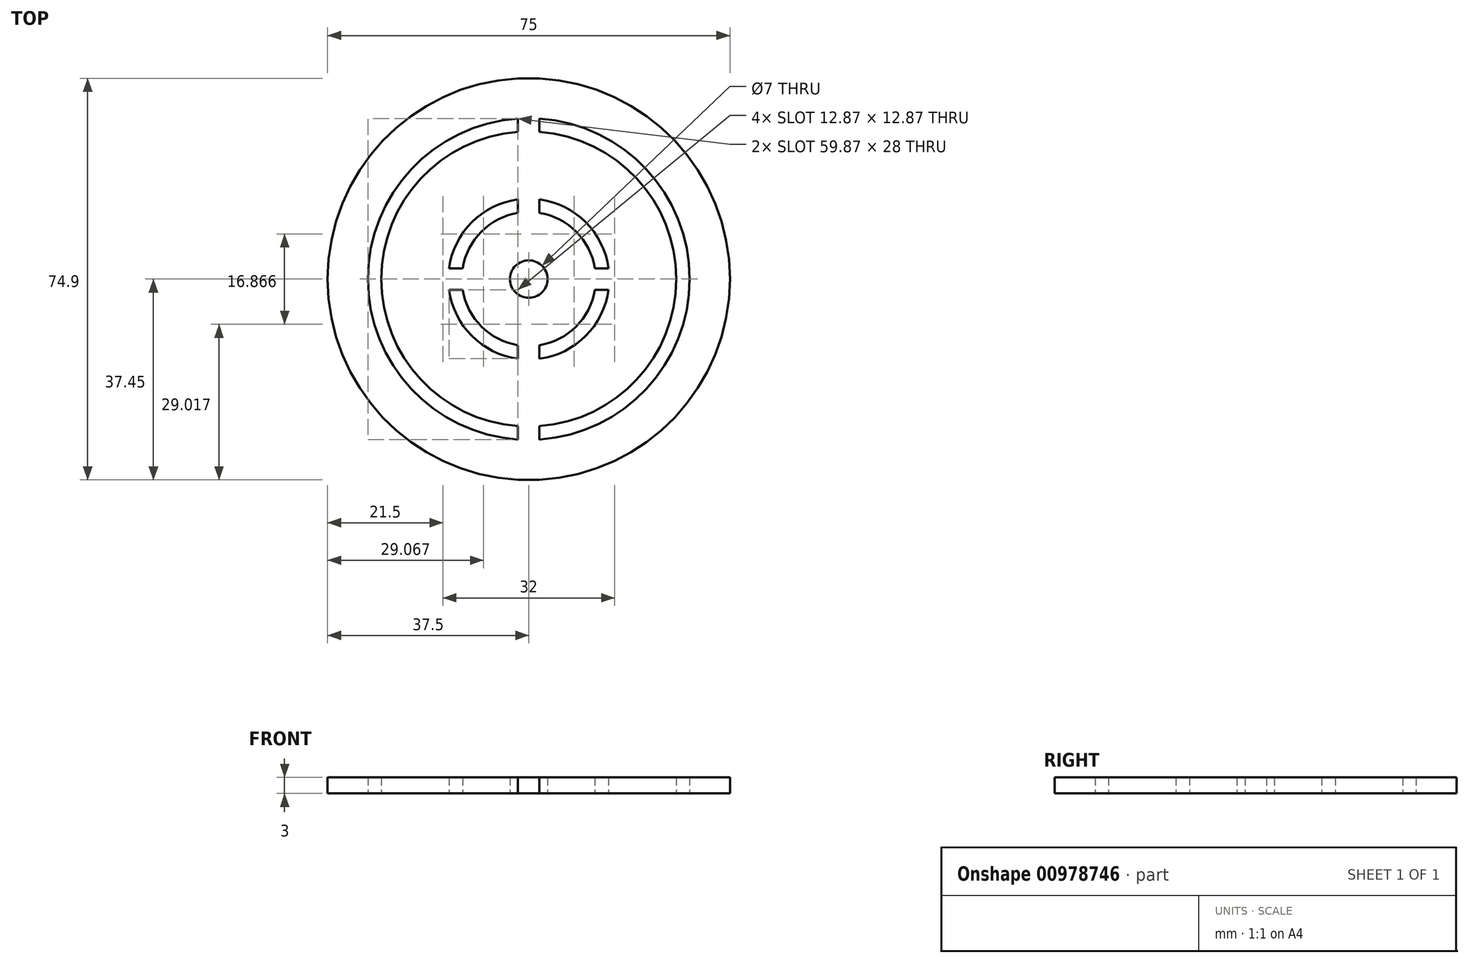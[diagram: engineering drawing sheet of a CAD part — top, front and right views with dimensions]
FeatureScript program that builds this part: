
annotation { "Feature Type Name" : "Feature", "Feature Type Description" : "" }
export const myFeature = defineFeature(function(context is Context, id is Id, definition is map)
    precondition{}
    {
        {
            var Q0;
            Q0=qCreatedBy(makeId("Top.planeOp"),FACE);
            var sketch = newSketch(context, id + "F0", { "sketchPlane" : qUnion([Q0])});
            skCircle(sketch, "E0", {"center": v(0, 0) * mm, "radius": 37.5 * mm});
            skCircle(sketch, "E1", {"center": v(0, 0) * mm, "radius": 3.5 * mm});
            skLineSegment(sketch, "E2", {"start": v(0, 0) * mm, "end": v(0, 37.5) * mm, "construction": true});
            skLineSegment(sketch, "E3", {"start": v(0, 0) * mm, "end": v(0, -37.5) * mm, "construction": true});
            skLineSegment(sketch, "E4", {"start": v(0, 0) * mm, "end": v(-37.5, 0) * mm, "construction": true});
            skLineSegment(sketch, "E5", {"start": v(0, 0) * mm, "end": v(37.5, 0) * mm, "construction": true});
            skCircle(sketch, "E6", {"center": v(0, 0) * mm, "radius": 30 * mm});
            skCircle(sketch, "E7", {"center": v(0, 0) * mm, "radius": 27.5 * mm});
            skLineSegment(sketch, "E8.bottom", {"start": v(-2, 2) * mm, "end": v(2, 2) * mm, "construction": true});
            skLineSegment(sketch, "E8.top", {"start": v(-2, -2) * mm, "end": v(2, -2) * mm, "construction": true});
            skLineSegment(sketch, "E8.left", {"start": v(-2, 2) * mm, "end": v(-2, -2) * mm, "construction": true});
            skLineSegment(sketch, "E8.right", {"start": v(2, 2) * mm, "end": v(2, -2) * mm, "construction": true});
            skLineSegment(sketch, "E9", {"start": v(-2, 2) * mm, "end": v(2, -2) * mm, "construction": true});
            skLineSegment(sketch, "E10.left", {"start": v(-2, 2) * mm, "end": v(-2, 0.65) * mm, "construction": true});
            skLineSegment(sketch, "E10.right", {"start": v(-37.45, -0.65) * mm, "end": v(-37.45, -2) * mm, "construction": true});
            skLineSegment(sketch, "E11.bottom", {"start": v(2, -2) * mm, "end": v(37.5, -2) * mm});
            skLineSegment(sketch, "E11.top", {"start": v(2, 2) * mm, "end": v(37.5, 2) * mm});
            skLineSegment(sketch, "E11.left", {"start": v(2, -2) * mm, "end": v(2, 2) * mm, "construction": true});
            skLineSegment(sketch, "E11.right", {"start": v(37.5, -2) * mm, "end": v(37.5, 2) * mm, "construction": true});
            skLineSegment(sketch, "E12.bottom", {"start": v(-2, 2) * mm, "end": v(-37.45, 2) * mm});
            skLineSegment(sketch, "E12.top", {"start": v(-2, -2) * mm, "end": v(-37.45, -2) * mm});
            skLineSegment(sketch, "E12.right", {"start": v(-37.45, 2) * mm, "end": v(-37.45, -2) * mm, "construction": true});
            skLineSegment(sketch, "E13.bottom", {"start": v(-2, 2) * mm, "end": v(2, 2) * mm});
            skLineSegment(sketch, "E13.top", {"start": v(-2, 37.45) * mm, "end": v(2, 37.45) * mm});
            skLineSegment(sketch, "E13.left", {"start": v(-2, 2) * mm, "end": v(-2, 37.45) * mm});
            skLineSegment(sketch, "E13.right", {"start": v(2, 2) * mm, "end": v(2, 37.45) * mm});
            skLineSegment(sketch, "E14.bottom", {"start": v(-2, -2) * mm, "end": v(2, -2) * mm});
            skLineSegment(sketch, "E14.top", {"start": v(-2, -37.45) * mm, "end": v(2, -37.45) * mm});
            skLineSegment(sketch, "E14.left", {"start": v(-2, -2) * mm, "end": v(-2, -37.45) * mm});
            skLineSegment(sketch, "E14.right", {"start": v(2, -2) * mm, "end": v(2, -37.45) * mm});
            skCircle(sketch, "E15", {"center": v(0, 0) * mm, "radius": 15 * mm});
            skCircle(sketch, "E16", {"center": v(0, 0) * mm, "radius": 12.5 * mm});
            skSolve(sketch);
        }
        {
            var Q0;
            {var subQ0=sQuery(id+"F0.wireOp",EDGE,"E13.left");var subQ5=sQuery(id+"F0.wireOp",EDGE,"E6");var subQ6=makeQuery(id+"F0.imprint","INTERSECT",VERTEX,{"derivedFrom":[subQ5,subQ0]});Q0=makeQuery(id+"F0.imprint","IMPRINT",FACE,{"disambiguationData":[TD([[makeQuery(id+"F0.imprint","IMPRINT",EDGE,{"disambiguationData":[TD([[subQ6,-1.0]])],"derivedFrom":subQ5}),-1.0]])]});}
            var Q1;
            {var subQ0=sQuery(id+"F0.wireOp",EDGE,"E12.top");var subQ5=sQuery(id+"F0.wireOp",EDGE,"E6");var subQ6=makeQuery(id+"F0.imprint","INTERSECT",VERTEX,{"derivedFrom":[subQ5,subQ0]});Q1=makeQuery(id+"F0.imprint","IMPRINT",FACE,{"disambiguationData":[TD([[makeQuery(id+"F0.imprint","IMPRINT",EDGE,{"disambiguationData":[TD([[subQ6,-1.0]])],"derivedFrom":subQ5}),-1.0]])]});}
            var Q2;
            {var subQ0=sQuery(id+"F0.wireOp",EDGE,"E12.top");var subQ1=sQuery(id+"F0.wireOp",EDGE,"E7");var subQ2=makeQuery(id+"F0.imprint","INTERSECT",VERTEX,{"derivedFrom":[subQ1,subQ0]});Q2=makeQuery(id+"F0.imprint","IMPRINT",FACE,{"disambiguationData":[TD([[makeQuery(id+"F0.imprint","IMPRINT",EDGE,{"disambiguationData":[TD([[subQ2,-1.0]])],"derivedFrom":subQ1}),1.0]])]});}
            var Q3;
            {var subQ0=sQuery(id+"F0.wireOp",EDGE,"E13.left");var subQ1=sQuery(id+"F0.wireOp",EDGE,"E7");var subQ2=makeQuery(id+"F0.imprint","INTERSECT",VERTEX,{"derivedFrom":[subQ1,subQ0]});Q3=makeQuery(id+"F0.imprint","IMPRINT",FACE,{"disambiguationData":[TD([[makeQuery(id+"F0.imprint","IMPRINT",EDGE,{"disambiguationData":[TD([[subQ2,-1.0]])],"derivedFrom":subQ1}),1.0]])]});}
            var Q4;
            {var subQ0=sQuery(id+"F0.wireOp",EDGE,"E13.right");var subQ1=sQuery(id+"F0.wireOp",EDGE,"E7");var subQ2=makeQuery(id+"F0.imprint","INTERSECT",VERTEX,{"derivedFrom":[subQ1,subQ0]});Q4=makeQuery(id+"F0.imprint","IMPRINT",FACE,{"disambiguationData":[TD([[makeQuery(id+"F0.imprint","IMPRINT",EDGE,{"disambiguationData":[TD([[subQ2,1.0]])],"derivedFrom":subQ1}),1.0]])]});}
            var Q5;
            {var subQ0=sQuery(id+"F0.wireOp",EDGE,"E14.right");var subQ1=sQuery(id+"F0.wireOp",EDGE,"E7");var subQ2=makeQuery(id+"F0.imprint","INTERSECT",VERTEX,{"derivedFrom":[subQ1,subQ0]});Q5=makeQuery(id+"F0.imprint","IMPRINT",FACE,{"disambiguationData":[TD([[makeQuery(id+"F0.imprint","IMPRINT",EDGE,{"disambiguationData":[TD([[subQ2,-1.0]])],"derivedFrom":subQ1}),1.0]])]});}
            var Q6;
            {var subQ0=sQuery(id+"F0.wireOp",EDGE,"E14.right");var subQ5=sQuery(id+"F0.wireOp",EDGE,"E6");var subQ6=makeQuery(id+"F0.imprint","INTERSECT",VERTEX,{"derivedFrom":[subQ5,subQ0]});Q6=makeQuery(id+"F0.imprint","IMPRINT",FACE,{"disambiguationData":[TD([[makeQuery(id+"F0.imprint","IMPRINT",EDGE,{"disambiguationData":[TD([[subQ6,-1.0]])],"derivedFrom":subQ5}),-1.0]])]});}
            var Q7;
            {var subQ0=sQuery(id+"F0.wireOp",EDGE,"E13.right");var subQ5=sQuery(id+"F0.wireOp",EDGE,"E6");var subQ6=makeQuery(id+"F0.imprint","INTERSECT",VERTEX,{"derivedFrom":[subQ5,subQ0]});Q7=makeQuery(id+"F0.imprint","IMPRINT",FACE,{"disambiguationData":[TD([[makeQuery(id+"F0.imprint","IMPRINT",EDGE,{"disambiguationData":[TD([[subQ6,1.0]])],"derivedFrom":subQ5}),-1.0]])]});}
            var Q8;
            {var subQ0=sQuery(id+"F0.wireOp",EDGE,"E13.right");var subQ1=sQuery(id+"F0.wireOp",EDGE,"E7");var subQ2=makeQuery(id+"F0.imprint","INTERSECT",VERTEX,{"derivedFrom":[subQ1,subQ0]});Q8=makeQuery(id+"F0.imprint","IMPRINT",FACE,{"disambiguationData":[TD([[makeQuery(id+"F0.imprint","IMPRINT",EDGE,{"disambiguationData":[TD([[subQ2,-1.0]])],"derivedFrom":subQ1}),1.0]])]});}
            var Q9;
            {var subQ0=sQuery(id+"F0.wireOp",EDGE,"E13.right");var subQ1=sQuery(id+"F0.wireOp",EDGE,"E6");var subQ2=makeQuery(id+"F0.imprint","INTERSECT",VERTEX,{"derivedFrom":[subQ1,subQ0]});Q9=makeQuery(id+"F0.imprint","IMPRINT",FACE,{"disambiguationData":[TD([[makeQuery(id+"F0.imprint","IMPRINT",EDGE,{"disambiguationData":[TD([[subQ2,-1.0]])],"derivedFrom":subQ1}),1.0]])]});}
            var Q10;
            {var subQ5=sQuery(id+"F0.wireOp",EDGE,"E13.top");Q10=makeQuery(id+"F0.imprint","IMPRINT",FACE,{"disambiguationData":[TD([[makeQuery(id+"F0.imprint","IMPRINT",EDGE,{"derivedFrom":subQ5}),-1.0]])]});}
            var Q11;
            {var subQ0=sQuery(id+"F0.wireOp",EDGE,"E16");var subQ1=sQuery(id+"F0.wireOp",EDGE,"E13.left");var subQ2=makeQuery(id+"F0.imprint","INTERSECT",VERTEX,{"derivedFrom":[subQ1,subQ0]});Q11=makeQuery(id+"F0.imprint","IMPRINT",FACE,{"disambiguationData":[TD([[makeQuery(id+"F0.imprint","IMPRINT",EDGE,{"disambiguationData":[TD([[subQ2,-1.0]])],"derivedFrom":subQ1}),-1.0]])]});}
            var Q12;
            {var subQ0=sQuery(id+"F0.wireOp",EDGE,"E13.right");var subQ1=sQuery(id+"F0.wireOp",EDGE,"E1");var subQ2=makeQuery(id+"F0.imprint","INTERSECT",VERTEX,{"derivedFrom":[subQ1,subQ0]});Q12=makeQuery(id+"F0.imprint","IMPRINT",FACE,{"disambiguationData":[TD([[makeQuery(id+"F0.imprint","IMPRINT",EDGE,{"disambiguationData":[TD([[subQ2,-1.0]])],"derivedFrom":subQ1}),-1.0]])]});}
            var Q13;
            {var subQ0=sQuery(id+"F0.wireOp",EDGE,"E12.top");var subQ1=sQuery(id+"F0.wireOp",EDGE,"E1");var subQ2=makeQuery(id+"F0.imprint","INTERSECT",VERTEX,{"derivedFrom":[subQ1,subQ0]});Q13=makeQuery(id+"F0.imprint","IMPRINT",FACE,{"disambiguationData":[TD([[makeQuery(id+"F0.imprint","IMPRINT",EDGE,{"disambiguationData":[TD([[subQ2,1.0]])],"derivedFrom":subQ1}),-1.0]])]});}
            var Q14;
            {var subQ0=sQuery(id+"F0.wireOp",EDGE,"E12.bottom");var subQ1=sQuery(id+"F0.wireOp",EDGE,"E7");var subQ2=makeQuery(id+"F0.imprint","INTERSECT",VERTEX,{"derivedFrom":[subQ1,subQ0]});Q14=makeQuery(id+"F0.imprint","IMPRINT",FACE,{"disambiguationData":[TD([[makeQuery(id+"F0.imprint","IMPRINT",EDGE,{"disambiguationData":[TD([[subQ2,-1.0]])],"derivedFrom":subQ1}),1.0]])]});}
            var Q15;
            {var subQ0=sQuery(id+"F0.wireOp",EDGE,"E16");var subQ1=sQuery(id+"F0.wireOp",EDGE,"E12.bottom");var subQ2=makeQuery(id+"F0.imprint","INTERSECT",VERTEX,{"derivedFrom":[subQ1,subQ0]});Q15=makeQuery(id+"F0.imprint","IMPRINT",FACE,{"disambiguationData":[TD([[makeQuery(id+"F0.imprint","IMPRINT",EDGE,{"disambiguationData":[TD([[subQ2,-1.0]])],"derivedFrom":subQ1}),1.0]])]});}
            var Q16;
            {var subQ0=sQuery(id+"F0.wireOp",EDGE,"E13.left");var subQ1=sQuery(id+"F0.wireOp",EDGE,"E1");var subQ2=makeQuery(id+"F0.imprint","INTERSECT",VERTEX,{"derivedFrom":[subQ1,subQ0]});Q16=makeQuery(id+"F0.imprint","IMPRINT",FACE,{"disambiguationData":[TD([[makeQuery(id+"F0.imprint","IMPRINT",EDGE,{"disambiguationData":[TD([[subQ2,-1.0]])],"derivedFrom":subQ1}),-1.0]])]});}
            var Q17;
            {var subQ0=sQuery(id+"F0.wireOp",EDGE,"E12.top");var subQ1=sQuery(id+"F0.wireOp",EDGE,"E1");var subQ2=makeQuery(id+"F0.imprint","INTERSECT",VERTEX,{"derivedFrom":[subQ1,subQ0]});Q17=makeQuery(id+"F0.imprint","IMPRINT",FACE,{"disambiguationData":[TD([[makeQuery(id+"F0.imprint","IMPRINT",EDGE,{"disambiguationData":[TD([[subQ2,-1.0]])],"derivedFrom":subQ1}),-1.0]])]});}
            var Q18;
            {var subQ0=sQuery(id+"F0.wireOp",EDGE,"E13.right");var subQ1=sQuery(id+"F0.wireOp",EDGE,"E1");var subQ2=makeQuery(id+"F0.imprint","INTERSECT",VERTEX,{"derivedFrom":[subQ1,subQ0]});Q18=makeQuery(id+"F0.imprint","IMPRINT",FACE,{"disambiguationData":[TD([[makeQuery(id+"F0.imprint","IMPRINT",EDGE,{"disambiguationData":[TD([[subQ2,1.0]])],"derivedFrom":subQ1}),-1.0]])]});}
            var Q19;
            {var subQ0=sQuery(id+"F0.wireOp",EDGE,"E14.right");var subQ1=sQuery(id+"F0.wireOp",EDGE,"E1");var subQ2=makeQuery(id+"F0.imprint","INTERSECT",VERTEX,{"derivedFrom":[subQ1,subQ0]});Q19=makeQuery(id+"F0.imprint","IMPRINT",FACE,{"disambiguationData":[TD([[makeQuery(id+"F0.imprint","IMPRINT",EDGE,{"disambiguationData":[TD([[subQ2,-1.0]])],"derivedFrom":subQ1}),-1.0]])]});}
            var Q20;
            {var subQ0=sQuery(id+"F0.wireOp",EDGE,"E14.left");var subQ1=sQuery(id+"F0.wireOp",EDGE,"E1");var subQ2=makeQuery(id+"F0.imprint","INTERSECT",VERTEX,{"derivedFrom":[subQ1,subQ0]});Q20=makeQuery(id+"F0.imprint","IMPRINT",FACE,{"disambiguationData":[TD([[makeQuery(id+"F0.imprint","IMPRINT",EDGE,{"disambiguationData":[TD([[subQ2,-1.0]])],"derivedFrom":subQ1}),-1.0]])]});}
            var Q21;
            {var subQ0=sQuery(id+"F0.wireOp",EDGE,"E16");var subQ1=sQuery(id+"F0.wireOp",EDGE,"E14.left");var subQ2=makeQuery(id+"F0.imprint","INTERSECT",VERTEX,{"derivedFrom":[subQ1,subQ0]});Q21=makeQuery(id+"F0.imprint","IMPRINT",FACE,{"disambiguationData":[TD([[makeQuery(id+"F0.imprint","IMPRINT",EDGE,{"disambiguationData":[TD([[subQ2,-1.0]])],"derivedFrom":subQ1}),1.0]])]});}
            var Q22;
            {var subQ0=sQuery(id+"F0.wireOp",EDGE,"E14.left");var subQ1=sQuery(id+"F0.wireOp",EDGE,"E7");var subQ2=makeQuery(id+"F0.imprint","INTERSECT",VERTEX,{"derivedFrom":[subQ1,subQ0]});Q22=makeQuery(id+"F0.imprint","IMPRINT",FACE,{"disambiguationData":[TD([[makeQuery(id+"F0.imprint","IMPRINT",EDGE,{"disambiguationData":[TD([[subQ2,-1.0]])],"derivedFrom":subQ1}),1.0]])]});}
            var Q23;
            {var subQ5=sQuery(id+"F0.wireOp",EDGE,"E14.top");Q23=makeQuery(id+"F0.imprint","IMPRINT",FACE,{"disambiguationData":[TD([[makeQuery(id+"F0.imprint","IMPRINT",EDGE,{"derivedFrom":subQ5}),1.0]])]});}
            var Q24;
            {var subQ0=sQuery(id+"F0.wireOp",EDGE,"E14.left");var subQ1=sQuery(id+"F0.wireOp",EDGE,"E6");var subQ2=makeQuery(id+"F0.imprint","INTERSECT",VERTEX,{"derivedFrom":[subQ1,subQ0]});Q24=makeQuery(id+"F0.imprint","IMPRINT",FACE,{"disambiguationData":[TD([[makeQuery(id+"F0.imprint","IMPRINT",EDGE,{"disambiguationData":[TD([[subQ2,-1.0]])],"derivedFrom":subQ1}),1.0]])]});}
            var Q25;
            {var subQ0=sQuery(id+"F0.wireOp",EDGE,"E16");var subQ1=sQuery(id+"F0.wireOp",EDGE,"E11.bottom");var subQ2=makeQuery(id+"F0.imprint","INTERSECT",VERTEX,{"derivedFrom":[subQ1,subQ0]});Q25=makeQuery(id+"F0.imprint","IMPRINT",FACE,{"disambiguationData":[TD([[makeQuery(id+"F0.imprint","IMPRINT",EDGE,{"disambiguationData":[TD([[subQ2,-1.0]])],"derivedFrom":subQ1}),1.0]])]});}
            var Q26;
            {var subQ0=sQuery(id+"F0.wireOp",EDGE,"E11.top");var subQ1=sQuery(id+"F0.wireOp",EDGE,"E1");var subQ2=makeQuery(id+"F0.imprint","INTERSECT",VERTEX,{"derivedFrom":[subQ1,subQ0]});Q26=makeQuery(id+"F0.imprint","IMPRINT",FACE,{"disambiguationData":[TD([[makeQuery(id+"F0.imprint","IMPRINT",EDGE,{"disambiguationData":[TD([[subQ2,1.0]])],"derivedFrom":subQ1}),-1.0]])]});}
            var Q27;
            {var subQ0=sQuery(id+"F0.wireOp",EDGE,"E11.top");var subQ1=sQuery(id+"F0.wireOp",EDGE,"E7");var subQ2=makeQuery(id+"F0.imprint","INTERSECT",VERTEX,{"derivedFrom":[subQ1,subQ0]});Q27=makeQuery(id+"F0.imprint","IMPRINT",FACE,{"disambiguationData":[TD([[makeQuery(id+"F0.imprint","IMPRINT",EDGE,{"disambiguationData":[TD([[subQ2,1.0]])],"derivedFrom":subQ1}),1.0]])]});}
            var Q28;
            {var subQ0=sQuery(id+"F0.wireOp",EDGE,"E11.top");var subQ1=sQuery(id+"F0.wireOp",EDGE,"E0");var subQ2=makeQuery(id+"F0.imprint","INTERSECT",VERTEX,{"derivedFrom":[subQ1,subQ0]});Q28=makeQuery(id+"F0.imprint","IMPRINT",FACE,{"disambiguationData":[TD([[makeQuery(id+"F0.imprint","IMPRINT",EDGE,{"disambiguationData":[TD([[subQ2,1.0]])],"derivedFrom":subQ1}),1.0]])]});}
            var Q29;
            {var subQ0=sQuery(id+"F0.wireOp",EDGE,"E12.top");var subQ1=sQuery(id+"F0.wireOp",EDGE,"E0");var subQ2=makeQuery(id+"F0.imprint","INTERSECT",VERTEX,{"derivedFrom":[subQ1,subQ0]});Q29=makeQuery(id+"F0.imprint","IMPRINT",FACE,{"disambiguationData":[TD([[makeQuery(id+"F0.imprint","IMPRINT",EDGE,{"disambiguationData":[TD([[subQ2,1.0]])],"derivedFrom":subQ1}),1.0]])]});}
            extrude(context, id + "F1", {"entities" : qUnion([Q0, Q1, Q2, Q3, Q4, Q5, Q6, Q7, Q8, Q9, Q10, Q11, Q12, Q13, Q14, Q15, Q16, Q17, Q18, Q19, Q20, Q21, Q22, Q23, Q24, Q25, Q26, Q27, Q28, Q29]), "depth" : 3 * mm, "offsetDistance" : 25 * mm});
        }
    });
